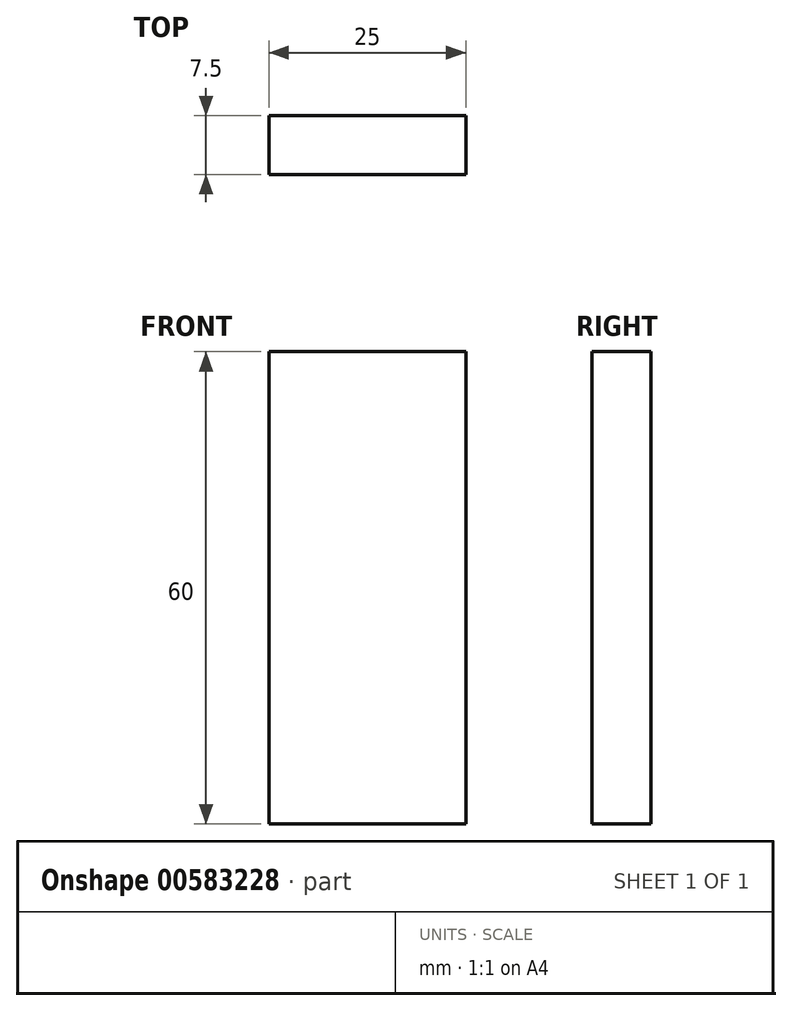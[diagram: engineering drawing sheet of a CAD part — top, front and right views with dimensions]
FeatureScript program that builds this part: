
annotation { "Feature Type Name" : "Feature", "Feature Type Description" : "" }
export const myFeature = defineFeature(function(context is Context, id is Id, definition is map)
    precondition{}
    {
        {
            var Q0;
            Q0=qCreatedBy(makeId("Front.planeOp"),FACE);
            var sketch = newSketch(context, id + "F0", { "sketchPlane" : qUnion([Q0])});
            skLineSegment(sketch, "E0.bottom", {"start": v(12.5, -30) * mm, "end": v(-12.5, -30) * mm});
            skLineSegment(sketch, "E0.top", {"start": v(12.5, 30) * mm, "end": v(-12.5, 30) * mm});
            skLineSegment(sketch, "E0.left", {"start": v(12.5, -30) * mm, "end": v(12.5, 30) * mm});
            skLineSegment(sketch, "E0.right", {"start": v(-12.5, -30) * mm, "end": v(-12.5, 30) * mm});
            skPoint(sketch, "E0.middle", {"position": v(0, 0) * mm});
            skSolve(sketch);
        }
        {
            var Q0;
            Q0=qSketchRegion(id+"F0",true);
            extrude(context, id + "F1", {"entities" : qUnion([Q0]), "endBound" : BoundingType.SYMMETRIC, "depth" : 7.5 * mm, "offsetDistance" : 25 * mm});
        }
    });
